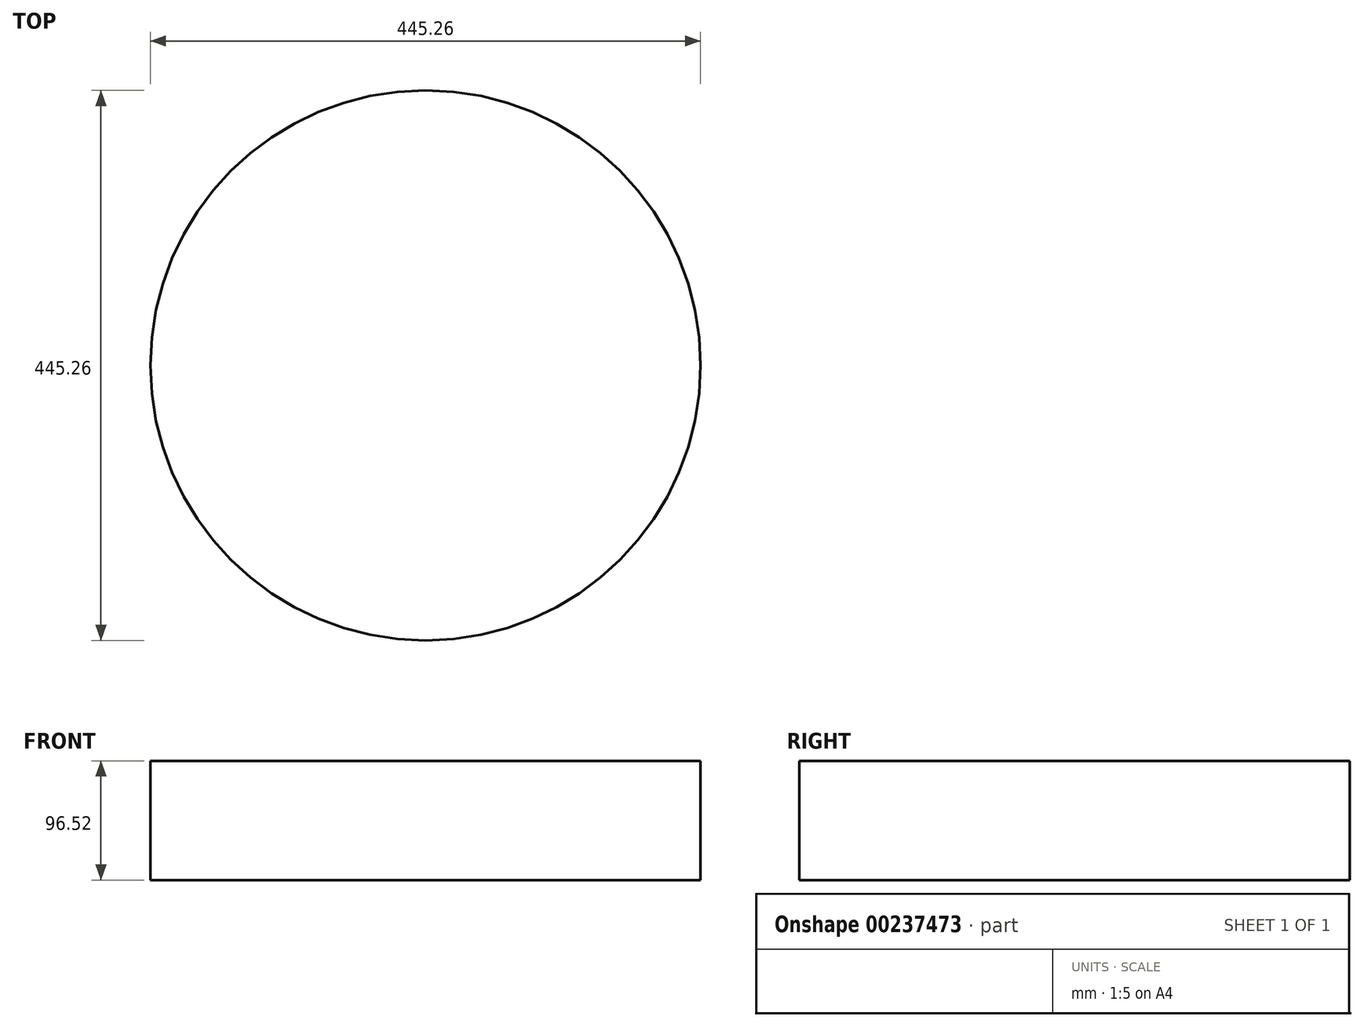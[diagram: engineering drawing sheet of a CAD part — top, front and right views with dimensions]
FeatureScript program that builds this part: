
annotation { "Feature Type Name" : "Feature", "Feature Type Description" : "" }
export const myFeature = defineFeature(function(context is Context, id is Id, definition is map)
    precondition{}
    {
        {
            var Q0;
            Q0=qCreatedBy(makeId("Top.planeOp"),FACE);
            var sketch = newSketch(context, id + "F0", { "sketchPlane" : qUnion([Q0])});
            skCircle(sketch, "E0", {"center": v(0, 0) * mm, "radius": 222.63 * mm});
            skSolve(sketch);
        }
        {
            var Q0;
            Q0=makeQuery(id+"F0.imprint","IMPRINT",FACE,{"disambiguationData":[TD([[makeQuery(id+"F0.imprint","IMPRINT",EDGE,{"derivedFrom":sQuery(id+"F0.wireOp",EDGE,"E0")}),1.0]])]});
            extrude(context, id + "F1", {"entities" : qUnion([Q0]), "depth" : 96.52 * mm});
        }
    });
